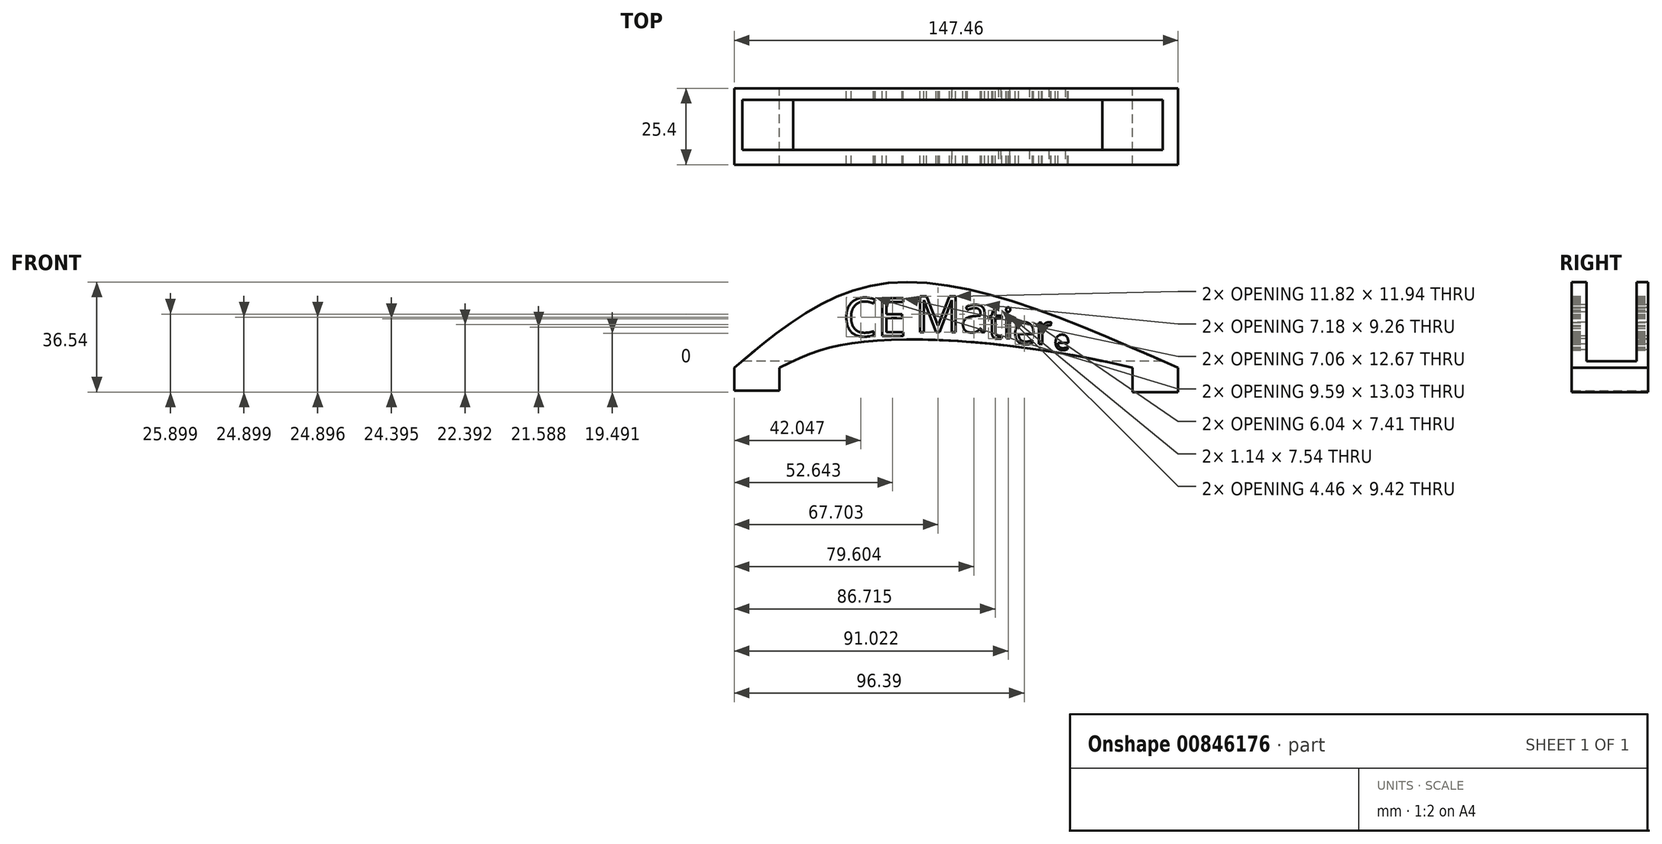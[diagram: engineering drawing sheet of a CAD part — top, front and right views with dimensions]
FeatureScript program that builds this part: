
annotation { "Feature Type Name" : "Feature", "Feature Type Description" : "" }
export const myFeature = defineFeature(function(context is Context, id is Id, definition is map)
    precondition{}
    {
        {
            var Q0;
            Q0=qCreatedBy(makeId("Front.planeOp"),FACE);
            var sketch = newSketch(context, id + "F0", { "sketchPlane" : qUnion([Q0])});
            skLineSegment(sketch, "E0.bottom", {"start": v(-72.47, 0) * mm, "end": v(-57.4, 0) * mm});
            skLineSegment(sketch, "E0.top", {"start": v(-72.47, -7.54) * mm, "end": v(-57.4, -7.54) * mm});
            skLineSegment(sketch, "E0.left", {"start": v(-72.47, 0) * mm, "end": v(-72.47, -7.54) * mm});
            skLineSegment(sketch, "E0.right", {"start": v(-57.4, 0) * mm, "end": v(-57.4, -7.54) * mm});
            skLineSegment(sketch, "E1.bottom", {"start": v(59.91, 0) * mm, "end": v(74.99, 0) * mm});
            skLineSegment(sketch, "E1.top", {"start": v(59.91, -8.04) * mm, "end": v(74.99, -8.04) * mm});
            skLineSegment(sketch, "E1.left", {"start": v(59.91, 0) * mm, "end": v(59.91, -8.04) * mm});
            skLineSegment(sketch, "E1.right", {"start": v(74.99, 0) * mm, "end": v(74.99, -8.04) * mm});
            skFitSpline(sketch, "E2", {"points": [v(-57.4, 0) * mm, v(-26.07, 9.01) * mm, v(59.91, 0) * mm], "startDerivative": vector(79.07, 41.59) * mm, "endDerivative": vector(151, -36.62) * mm});
            skFitSpline(sketch, "E3", {"points": [v(-72.47, 0) * mm, v(-21.73, 28.14) * mm, v(74.99, 0) * mm], "startDerivative": vector(106.27, 89.95) * mm, "endDerivative": vector(185.05, -82.1) * mm});
            skText(sketch, "E4", { "text": "Ma\n", "fontName": "OpenSans-Regular.ttf"});
            skText(sketch, "E5", { "text": "ti", "fontName": "OpenSans-Regular.ttf"});
            skText(sketch, "E6", { "text": "er\n", "fontName": "OpenSans-Regular.ttf"});
            skText(sketch, "E7", { "text": "e", "fontName": "OpenSans-Regular.ttf"});
            skText(sketch, "E8", { "text": "CE\n", "fontName": "OpenSans-Regular.ttf"});
            const initialGuessF0  = {"E4": [-0.01232, 0.01189, 1, 0, 0.01204], "E5": [0.0118, 0.00978, 1, 0, 0.01014], "E6": [0.02015, 0.00788, 1, 0, 0.00961], "E7": [0.03377, 0.00597, 1, 0, 0.0067], "E8": [-0.0363, 0.01052, 1, 0, 0.01278]};
            skSetInitialGuess(sketch, initialGuessF0);
            skSolve(sketch);
        }
        {
            var Q0;
            Q0=makeQuery(id+"F0.imprint","IMPRINT",FACE,{"disambiguationData":[TD([[makeQuery(id+"F0.imprint","IMPRINT",EDGE,{"derivedFrom":sQuery(id+"F0.wireOp",EDGE,"E0.bottom")}),-1.0]])]});
            var Q1;
            Q1=makeQuery(id+"F0.imprint","IMPRINT",FACE,{"disambiguationData":[TD([[makeQuery(id+"F0.imprint","IMPRINT",EDGE,{"derivedFrom":sQuery(id+"F0.wireOp",EDGE,"E1.bottom")}),-1.0]])]});
            var Q2;
            Q2=makeQuery(id+"F0.imprint","IMPRINT",FACE,{"disambiguationData":[TD([[makeQuery(id+"F0.imprint","IMPRINT",EDGE,{"derivedFrom":sQuery(id+"F0.wireOp",EDGE,"E0.bottom")}),1.0]])]});
            extrude(context, id + "F1", {"entities" : qUnion([Q0, Q1, Q2]), "depth" : 25.4 * mm, "offsetDistance" : 25.4 * mm});
        }
        {
            var Q0;
            Q0=qCreatedBy(makeId("Right.planeOp"),FACE);
            var sketch = newSketch(context, id + "F2", { "sketchPlane" : qUnion([Q0])});
            skLineSegment(sketch, "E9.bottom", {"start": v(-20.47, 32.92) * mm, "end": v(-3.9, 32.92) * mm});
            skLineSegment(sketch, "E9.top", {"start": v(-20.47, 2.26) * mm, "end": v(-3.9, 2.26) * mm});
            skLineSegment(sketch, "E9.left", {"start": v(-20.47, 32.92) * mm, "end": v(-20.47, 2.26) * mm});
            skLineSegment(sketch, "E9.right", {"start": v(-3.9, 32.92) * mm, "end": v(-3.9, 2.26) * mm});
            skSolve(sketch);
        }
        {
            var Q0;
            Q0=makeQuery(id+"F2.imprint","IMPRINT",FACE,{"disambiguationData":[TD([[makeQuery(id+"F2.imprint","IMPRINT",EDGE,{"derivedFrom":sQuery(id+"F2.wireOp",EDGE,"E9.bottom")}),-1.0]])]});
            extrude(context, id + "F3", {"entities" : qUnion([Q0]), "operationType" : NewBodyOperationType.REMOVE, "depth" : 111.25 * mm, "offsetDistance" : 25.4 * mm, "hasSecondDirection" : true, "secondDirectionOppositeDirection" : true, "secondDirectionDepth" : 113.8 * mm});
        }
    });
